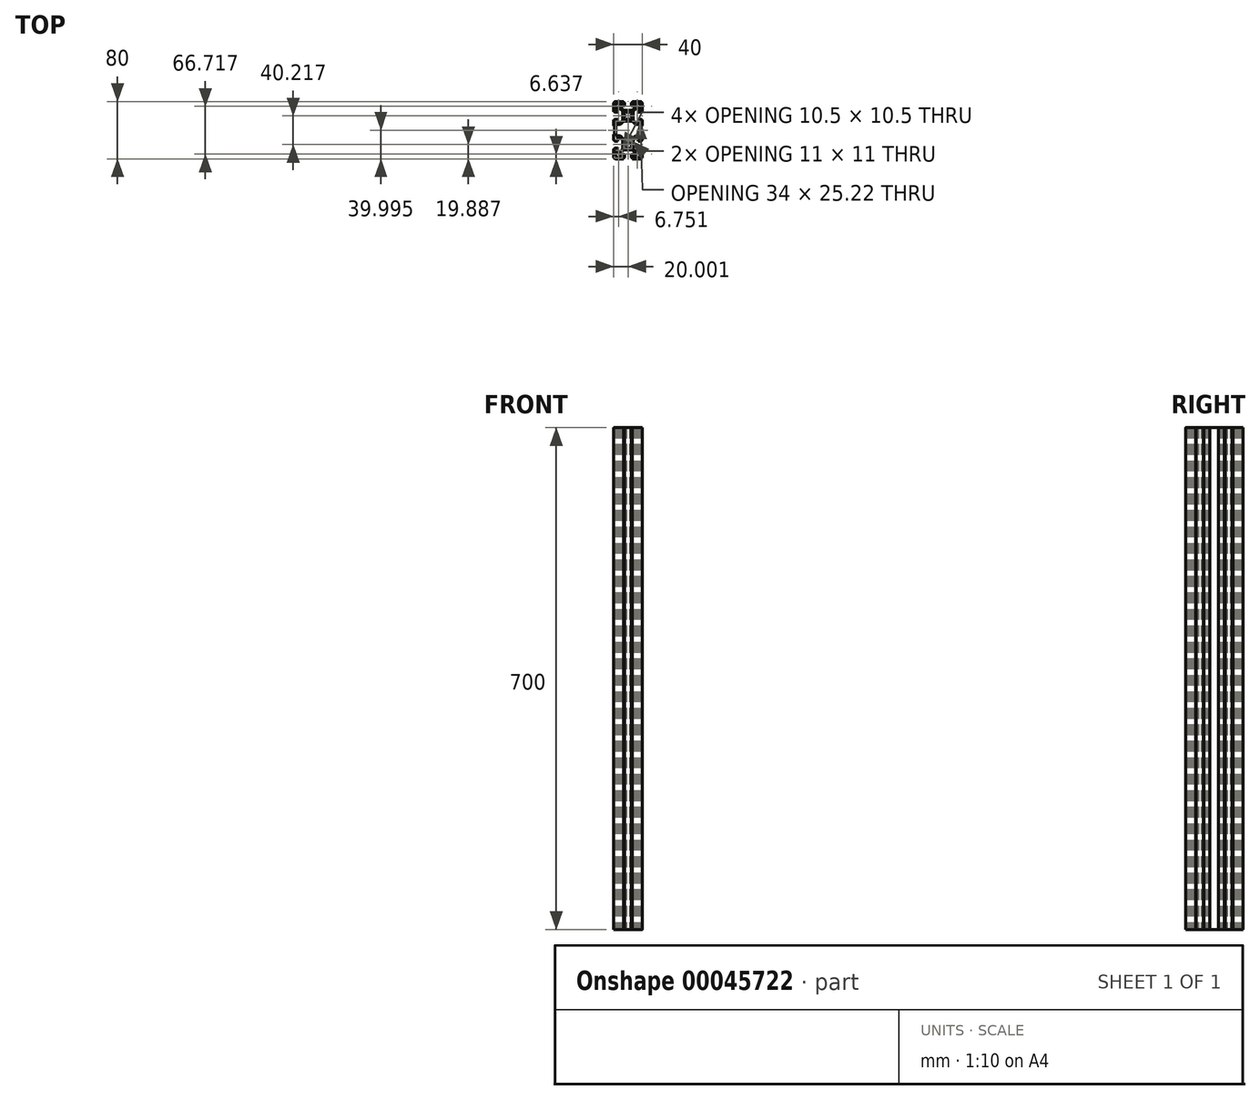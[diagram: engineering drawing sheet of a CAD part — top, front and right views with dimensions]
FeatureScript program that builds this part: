
annotation { "Feature Type Name" : "Feature", "Feature Type Description" : "" }
export const myFeature = defineFeature(function(context is Context, id is Id, definition is map)
    precondition{}
    {
        {
            var Q0;
            Q0=qCreatedBy(makeId("Top.planeOp"),FACE);
            var sketch = newSketch(context, id + "F0", { "sketchPlane" : qUnion([Q0])});
            skLineSegment(sketch, "E0", {"start": v(-19.67, 37.28) * mm, "end": v(-19.67, 26.18) * mm});
            skLineSegment(sketch, "E1", {"start": v(-19.67, 26.18) * mm, "end": v(-18.17, 26.18) * mm});
            skLineSegment(sketch, "E2", {"start": v(-18.17, 26.18) * mm, "end": v(-18.17, 25.38) * mm});
            skLineSegment(sketch, "E3", {"start": v(-18.17, 25.38) * mm, "end": v(-13.67, 25.38) * mm});
            skLineSegment(sketch, "E4", {"start": v(-13.67, 25.38) * mm, "end": v(-13.67, 30.43) * mm});
            skLineSegment(sketch, "E5", {"start": v(-13.67, 30.43) * mm, "end": v(-11.13, 30.43) * mm});
            skLineSegment(sketch, "E6", {"start": v(-11.13, 30.43) * mm, "end": v(-7.17, 26.47) * mm});
            skLineSegment(sketch, "E7", {"start": v(-7.17, 26.47) * mm, "end": v(-7.17, 14.3) * mm});
            skLineSegment(sketch, "E8", {"start": v(-7.17, 14.3) * mm, "end": v(-11.13, 10.33) * mm});
            skLineSegment(sketch, "E9", {"start": v(-11.13, 10.33) * mm, "end": v(-13.67, 10.33) * mm});
            skLineSegment(sketch, "E10", {"start": v(-13.67, 10.33) * mm, "end": v(-13.67, 15.38) * mm});
            skLineSegment(sketch, "E11", {"start": v(-13.67, 15.38) * mm, "end": v(-18.17, 15.38) * mm});
            skLineSegment(sketch, "E12", {"start": v(-18.17, 15.38) * mm, "end": v(-18.17, 14.58) * mm});
            skLineSegment(sketch, "E13", {"start": v(-18.17, 14.58) * mm, "end": v(-19.67, 14.58) * mm});
            skLineSegment(sketch, "E14", {"start": v(-19.67, 14.58) * mm, "end": v(-19.67, 6.38) * mm});
            skLineSegment(sketch, "E15", {"start": v(-19.67, 6.38) * mm, "end": v(-18.67, 6.38) * mm});
            skLineSegment(sketch, "E16", {"start": v(-18.67, 6.38) * mm, "end": v(-18.67, -5.83) * mm});
            skLineSegment(sketch, "E17", {"start": v(-18.67, -5.83) * mm, "end": v(-19.67, -5.83) * mm});
            skLineSegment(sketch, "E18", {"start": v(-19.67, -5.83) * mm, "end": v(-19.67, -14.03) * mm});
            skLineSegment(sketch, "E19", {"start": v(-19.67, -14.03) * mm, "end": v(-18.17, -14.03) * mm});
            skLineSegment(sketch, "E20", {"start": v(-18.17, -14.03) * mm, "end": v(-18.17, -14.83) * mm});
            skLineSegment(sketch, "E21", {"start": v(-18.17, -14.83) * mm, "end": v(-13.67, -14.83) * mm});
            skLineSegment(sketch, "E22", {"start": v(-13.67, -14.83) * mm, "end": v(-13.67, -9.78) * mm});
            skLineSegment(sketch, "E23", {"start": v(-13.67, -9.78) * mm, "end": v(-11.13, -9.78) * mm});
            skLineSegment(sketch, "E24", {"start": v(-11.13, -9.78) * mm, "end": v(-7.17, -13.75) * mm});
            skLineSegment(sketch, "E25", {"start": v(-7.17, -13.75) * mm, "end": v(-7.17, -25.92) * mm});
            skLineSegment(sketch, "E26", {"start": v(-7.17, -25.92) * mm, "end": v(-11.13, -29.88) * mm});
            skLineSegment(sketch, "E27", {"start": v(-11.13, -29.88) * mm, "end": v(-13.67, -29.88) * mm});
            skLineSegment(sketch, "E28", {"start": v(-13.67, -29.88) * mm, "end": v(-13.67, -24.83) * mm});
            skLineSegment(sketch, "E29", {"start": v(-13.67, -24.83) * mm, "end": v(-18.17, -24.83) * mm});
            skLineSegment(sketch, "E30", {"start": v(-18.17, -24.83) * mm, "end": v(-18.17, -25.63) * mm});
            skLineSegment(sketch, "E31", {"start": v(-18.17, -25.63) * mm, "end": v(-19.67, -25.63) * mm});
            skLineSegment(sketch, "E32", {"start": v(-19.67, -25.63) * mm, "end": v(-19.67, -36.72) * mm});
            skLineSegment(sketch, "E33", {"start": v(-16.67, -39.72) * mm, "end": v(-5.47, -39.72) * mm});
            skLineSegment(sketch, "E34", {"start": v(-5.47, -39.72) * mm, "end": v(-5.47, -38.22) * mm});
            skLineSegment(sketch, "E35", {"start": v(-5.47, -38.22) * mm, "end": v(-4.67, -38.22) * mm});
            skLineSegment(sketch, "E36", {"start": v(-4.67, -38.22) * mm, "end": v(-4.67, -33.72) * mm});
            skLineSegment(sketch, "E37", {"start": v(-4.67, -33.72) * mm, "end": v(-9.72, -33.72) * mm});
            skLineSegment(sketch, "E38", {"start": v(-9.72, -33.72) * mm, "end": v(-9.72, -31.19) * mm});
            skLineSegment(sketch, "E39", {"start": v(-9.72, -31.19) * mm, "end": v(-5.75, -27.22) * mm});
            skLineSegment(sketch, "E40", {"start": v(-5.75, -27.22) * mm, "end": v(6.42, -27.22) * mm});
            skLineSegment(sketch, "E41", {"start": v(6.42, -27.22) * mm, "end": v(10.38, -31.19) * mm});
            skLineSegment(sketch, "E42", {"start": v(10.38, -31.19) * mm, "end": v(10.38, -33.72) * mm});
            skLineSegment(sketch, "E43", {"start": v(10.38, -33.72) * mm, "end": v(5.33, -33.72) * mm});
            skLineSegment(sketch, "E44", {"start": v(5.33, -33.72) * mm, "end": v(5.33, -38.22) * mm});
            skLineSegment(sketch, "E45", {"start": v(5.33, -38.22) * mm, "end": v(6.13, -38.22) * mm});
            skLineSegment(sketch, "E46", {"start": v(6.13, -38.22) * mm, "end": v(6.13, -39.72) * mm});
            skLineSegment(sketch, "E47", {"start": v(6.13, -39.72) * mm, "end": v(17.33, -39.72) * mm});
            skLineSegment(sketch, "E48", {"start": v(20.33, -36.72) * mm, "end": v(20.33, -25.63) * mm});
            skLineSegment(sketch, "E49", {"start": v(20.33, -25.63) * mm, "end": v(18.83, -25.63) * mm});
            skLineSegment(sketch, "E50", {"start": v(18.83, -25.63) * mm, "end": v(18.83, -24.83) * mm});
            skLineSegment(sketch, "E51", {"start": v(18.83, -24.83) * mm, "end": v(14.33, -24.83) * mm});
            skLineSegment(sketch, "E52", {"start": v(14.33, -24.83) * mm, "end": v(14.33, -29.88) * mm});
            skLineSegment(sketch, "E53", {"start": v(14.33, -29.88) * mm, "end": v(11.8, -29.88) * mm});
            skLineSegment(sketch, "E54", {"start": v(11.8, -29.88) * mm, "end": v(7.83, -25.92) * mm});
            skLineSegment(sketch, "E55", {"start": v(7.83, -25.92) * mm, "end": v(7.83, -13.75) * mm});
            skLineSegment(sketch, "E56", {"start": v(7.83, -13.75) * mm, "end": v(11.8, -9.78) * mm});
            skLineSegment(sketch, "E57", {"start": v(11.8, -9.78) * mm, "end": v(14.33, -9.78) * mm});
            skLineSegment(sketch, "E58", {"start": v(14.33, -9.78) * mm, "end": v(14.33, -14.83) * mm});
            skLineSegment(sketch, "E59", {"start": v(14.33, -14.83) * mm, "end": v(18.83, -14.83) * mm});
            skLineSegment(sketch, "E60", {"start": v(18.83, -14.83) * mm, "end": v(18.83, -14.03) * mm});
            skLineSegment(sketch, "E61", {"start": v(18.83, -14.03) * mm, "end": v(20.33, -14.03) * mm});
            skLineSegment(sketch, "E62", {"start": v(20.33, -14.03) * mm, "end": v(20.33, -5.83) * mm});
            skLineSegment(sketch, "E63", {"start": v(20.33, -5.83) * mm, "end": v(19.33, -5.83) * mm});
            skLineSegment(sketch, "E64", {"start": v(19.33, -5.83) * mm, "end": v(19.33, 6.38) * mm});
            skLineSegment(sketch, "E65", {"start": v(19.33, 6.38) * mm, "end": v(20.33, 6.38) * mm});
            skLineSegment(sketch, "E66", {"start": v(20.33, 6.38) * mm, "end": v(20.33, 14.58) * mm});
            skLineSegment(sketch, "E67", {"start": v(20.33, 14.58) * mm, "end": v(18.83, 14.58) * mm});
            skLineSegment(sketch, "E68", {"start": v(18.83, 14.58) * mm, "end": v(18.83, 15.38) * mm});
            skLineSegment(sketch, "E69", {"start": v(18.83, 15.38) * mm, "end": v(14.33, 15.38) * mm});
            skLineSegment(sketch, "E70", {"start": v(14.33, 15.38) * mm, "end": v(14.33, 10.33) * mm});
            skLineSegment(sketch, "E71", {"start": v(14.33, 10.33) * mm, "end": v(11.8, 10.33) * mm});
            skLineSegment(sketch, "E72", {"start": v(11.8, 10.33) * mm, "end": v(7.83, 14.3) * mm});
            skLineSegment(sketch, "E73", {"start": v(7.83, 14.3) * mm, "end": v(7.83, 26.47) * mm});
            skLineSegment(sketch, "E74", {"start": v(7.83, 26.47) * mm, "end": v(11.8, 30.43) * mm});
            skLineSegment(sketch, "E75", {"start": v(11.8, 30.43) * mm, "end": v(14.33, 30.43) * mm});
            skLineSegment(sketch, "E76", {"start": v(14.33, 30.43) * mm, "end": v(14.33, 25.38) * mm});
            skLineSegment(sketch, "E77", {"start": v(14.33, 25.38) * mm, "end": v(18.83, 25.38) * mm});
            skLineSegment(sketch, "E78", {"start": v(18.83, 25.38) * mm, "end": v(18.83, 26.18) * mm});
            skLineSegment(sketch, "E79", {"start": v(18.83, 26.18) * mm, "end": v(20.33, 26.18) * mm});
            skLineSegment(sketch, "E80", {"start": v(20.33, 26.18) * mm, "end": v(20.33, 37.28) * mm});
            skLineSegment(sketch, "E81", {"start": v(17.33, 40.28) * mm, "end": v(6.13, 40.28) * mm});
            skLineSegment(sketch, "E82", {"start": v(6.13, 40.28) * mm, "end": v(6.13, 38.78) * mm});
            skLineSegment(sketch, "E83", {"start": v(6.13, 38.78) * mm, "end": v(5.33, 38.78) * mm});
            skLineSegment(sketch, "E84", {"start": v(5.33, 38.78) * mm, "end": v(5.33, 34.28) * mm});
            skLineSegment(sketch, "E85", {"start": v(5.33, 34.28) * mm, "end": v(10.38, 34.28) * mm});
            skLineSegment(sketch, "E86", {"start": v(10.38, 34.28) * mm, "end": v(10.38, 31.74) * mm});
            skLineSegment(sketch, "E87", {"start": v(10.38, 31.74) * mm, "end": v(6.42, 27.78) * mm});
            skLineSegment(sketch, "E88", {"start": v(6.42, 27.78) * mm, "end": v(-5.75, 27.78) * mm});
            skLineSegment(sketch, "E89", {"start": v(-5.75, 27.78) * mm, "end": v(-9.72, 31.74) * mm});
            skLineSegment(sketch, "E90", {"start": v(-9.72, 31.74) * mm, "end": v(-9.72, 34.28) * mm});
            skLineSegment(sketch, "E91", {"start": v(-9.72, 34.28) * mm, "end": v(-4.67, 34.28) * mm});
            skLineSegment(sketch, "E92", {"start": v(-4.67, 34.28) * mm, "end": v(-4.67, 38.78) * mm});
            skLineSegment(sketch, "E93", {"start": v(-4.67, 38.78) * mm, "end": v(-5.47, 38.78) * mm});
            skLineSegment(sketch, "E94", {"start": v(-5.47, 38.78) * mm, "end": v(-5.47, 40.28) * mm});
            skLineSegment(sketch, "E95", {"start": v(-5.47, 40.28) * mm, "end": v(-16.67, 40.28) * mm});
            skLineSegment(sketch, "E96", {"start": v(-14.17, 37.63) * mm, "end": v(-14.17, 38.88) * mm});
            skLineSegment(sketch, "E97", {"start": v(-14.17, 38.88) * mm, "end": v(-9.17, 38.88) * mm});
            skLineSegment(sketch, "E98", {"start": v(-9.17, 35.88) * mm, "end": v(-11.42, 35.88) * mm});
            skLineSegment(sketch, "E99", {"start": v(-15.17, 32.13) * mm, "end": v(-15.17, 29.88) * mm});
            skLineSegment(sketch, "E100", {"start": v(-16.92, 34.88) * mm, "end": v(-18.17, 34.88) * mm});
            skLineSegment(sketch, "E101", {"start": v(-18.17, 34.88) * mm, "end": v(-18.17, 29.88) * mm});
            skArc(sketch, "E102", {"start": v(-9.17, 35.88) * mm, "mid": v(-7.67, 37.38) * mm, "end": v(-9.17, 38.88) * mm});
            skArc(sketch, "E103", {"start": v(-18.17, 29.88) * mm, "mid": v(-16.67, 28.38) * mm, "end": v(-15.17, 29.88) * mm});
            skArc(sketch, "E104", {"start": v(-14.17, 37.63) * mm, "mid": v(-16.11, 36.83) * mm, "end": v(-16.92, 34.88) * mm});
            skArc(sketch, "E105", {"start": v(9.83, 38.88) * mm, "mid": v(8.33, 37.38) * mm, "end": v(9.83, 35.88) * mm});
            skArc(sketch, "E106", {"start": v(15.83, 29.88) * mm, "mid": v(17.33, 28.38) * mm, "end": v(18.83, 29.88) * mm});
            skArc(sketch, "E107", {"start": v(-4.25, 22.38) * mm, "mid": v(-4.67, 20.38) * mm, "end": v(-4.25, 18.39) * mm});
            skArc(sketch, "E108", {"start": v(-11.6, -35.33) * mm, "mid": v(-12.22, -32.39) * mm, "end": v(-15.17, -31.77) * mm});
            skArc(sketch, "E109", {"start": v(14.83, -37.08) * mm, "mid": v(16.78, -36.28) * mm, "end": v(17.58, -34.33) * mm});
            skArc(sketch, "E110", {"start": v(9.83, -35.33) * mm, "mid": v(8.33, -36.83) * mm, "end": v(9.83, -38.33) * mm});
            skArc(sketch, "E111", {"start": v(18.83, -29.33) * mm, "mid": v(17.33, -27.83) * mm, "end": v(15.83, -29.33) * mm});
            skArc(sketch, "E112", {"start": v(12.27, 35.88) * mm, "mid": v(12.89, 32.94) * mm, "end": v(15.83, 32.32) * mm});
            skLineSegment(sketch, "E113", {"start": v(-15.17, 32.13) * mm, "end": v(-15.17, 32.32) * mm});
            skLineSegment(sketch, "E114", {"start": v(-11.42, 35.88) * mm, "end": v(-11.6, 35.88) * mm});
            skLineSegment(sketch, "E115", {"start": v(9.83, 38.88) * mm, "end": v(14.83, 38.88) * mm});
            skLineSegment(sketch, "E116", {"start": v(14.83, 38.88) * mm, "end": v(14.83, 37.63) * mm});
            skLineSegment(sketch, "E117", {"start": v(9.83, 35.88) * mm, "end": v(12.27, 35.88) * mm});
            skLineSegment(sketch, "E118", {"start": v(17.58, 34.88) * mm, "end": v(18.83, 34.88) * mm});
            skLineSegment(sketch, "E119", {"start": v(18.83, 34.88) * mm, "end": v(18.83, 29.88) * mm});
            skLineSegment(sketch, "E120", {"start": v(15.83, 29.88) * mm, "end": v(15.83, 32.32) * mm});
            skArc(sketch, "E121.trimOffspring", {"start": v(17.58, 34.88) * mm, "mid": v(16.78, 36.83) * mm, "end": v(14.83, 37.63) * mm});
            skArc(sketch, "E122.trimOffspring", {"start": v(-15.17, 32.32) * mm, "mid": v(-12.22, 32.94) * mm, "end": v(-11.6, 35.88) * mm});
            skLineSegment(sketch, "E123", {"start": v(-4.25, 22.38) * mm, "end": v(-5.17, 22.78) * mm});
            skLineSegment(sketch, "E124", {"start": v(-5.17, 22.78) * mm, "end": v(-5.17, 25.88) * mm});
            skLineSegment(sketch, "E125", {"start": v(-5.17, 25.88) * mm, "end": v(-2.07, 25.88) * mm});
            skLineSegment(sketch, "E126", {"start": v(-2.07, 25.88) * mm, "end": v(-1.67, 24.97) * mm});
            skLineSegment(sketch, "E127", {"start": v(2.33, 24.97) * mm, "end": v(2.73, 25.88) * mm});
            skLineSegment(sketch, "E128", {"start": v(2.73, 25.88) * mm, "end": v(5.83, 25.88) * mm});
            skLineSegment(sketch, "E129", {"start": v(5.83, 25.88) * mm, "end": v(5.83, 22.78) * mm});
            skLineSegment(sketch, "E130", {"start": v(-4.25, 18.39) * mm, "end": v(-5.17, 17.99) * mm});
            skLineSegment(sketch, "E131", {"start": v(-5.17, 17.99) * mm, "end": v(-5.17, 14.88) * mm});
            skLineSegment(sketch, "E132", {"start": v(-5.17, 14.88) * mm, "end": v(-2.07, 14.88) * mm});
            skLineSegment(sketch, "E133", {"start": v(-2.07, 14.88) * mm, "end": v(-1.67, 15.8) * mm});
            skLineSegment(sketch, "E134", {"start": v(2.33, 15.8) * mm, "end": v(2.73, 14.88) * mm});
            skLineSegment(sketch, "E135", {"start": v(2.73, 14.88) * mm, "end": v(5.83, 14.88) * mm});
            skLineSegment(sketch, "E136", {"start": v(5.83, 14.88) * mm, "end": v(5.83, 17.99) * mm});
            skArc(sketch, "E137.trimOffspring", {"start": v(2.33, 24.97) * mm, "mid": v(0.33, 25.38) * mm, "end": v(-1.67, 24.97) * mm});
            skArc(sketch, "E138.trimOffspring", {"start": v(4.91, 18.39) * mm, "mid": v(5.33, 20.38) * mm, "end": v(4.91, 22.38) * mm});
            skLineSegment(sketch, "E139", {"start": v(-16.67, 8.33) * mm, "end": v(-16.67, -7.78) * mm});
            skLineSegment(sketch, "E140", {"start": v(-16.67, -7.78) * mm, "end": v(-10.3, -7.78) * mm});
            skLineSegment(sketch, "E141", {"start": v(-10.3, -7.78) * mm, "end": v(-5.75, -12.33) * mm});
            skLineSegment(sketch, "E142", {"start": v(-5.75, -12.33) * mm, "end": v(6.42, -12.33) * mm});
            skLineSegment(sketch, "E143", {"start": v(6.42, -12.33) * mm, "end": v(10.97, -7.78) * mm});
            skLineSegment(sketch, "E144", {"start": v(10.97, -7.78) * mm, "end": v(17.33, -7.78) * mm});
            skLineSegment(sketch, "E145", {"start": v(17.33, -7.78) * mm, "end": v(17.33, 8.33) * mm});
            skLineSegment(sketch, "E146", {"start": v(17.33, 8.33) * mm, "end": v(10.97, 8.33) * mm});
            skLineSegment(sketch, "E147", {"start": v(10.97, 8.33) * mm, "end": v(6.42, 12.88) * mm});
            skLineSegment(sketch, "E148", {"start": v(6.42, 12.88) * mm, "end": v(-5.75, 12.88) * mm});
            skLineSegment(sketch, "E149", {"start": v(-5.75, 12.88) * mm, "end": v(-10.3, 8.33) * mm});
            skLineSegment(sketch, "E150", {"start": v(-10.3, 8.33) * mm, "end": v(-16.67, 8.33) * mm});
            skLineSegment(sketch, "E151", {"start": v(-1.67, -15.25) * mm, "end": v(-2.07, -14.33) * mm});
            skLineSegment(sketch, "E152", {"start": v(-2.07, -14.33) * mm, "end": v(-5.17, -14.33) * mm});
            skLineSegment(sketch, "E153", {"start": v(-5.17, -14.33) * mm, "end": v(-5.17, -17.44) * mm});
            skLineSegment(sketch, "E154", {"start": v(-5.17, -17.44) * mm, "end": v(-4.25, -17.84) * mm});
            skLineSegment(sketch, "E155", {"start": v(2.33, -15.25) * mm, "end": v(2.73, -14.33) * mm});
            skLineSegment(sketch, "E156", {"start": v(2.73, -14.33) * mm, "end": v(5.83, -14.33) * mm});
            skLineSegment(sketch, "E157", {"start": v(5.83, -14.33) * mm, "end": v(5.83, -17.44) * mm});
            skLineSegment(sketch, "E158", {"start": v(5.83, -17.44) * mm, "end": v(4.91, -17.84) * mm});
            skLineSegment(sketch, "E159", {"start": v(-4.25, -21.83) * mm, "end": v(-5.17, -22.23) * mm});
            skLineSegment(sketch, "E160", {"start": v(-5.17, -22.23) * mm, "end": v(-5.17, -25.33) * mm});
            skLineSegment(sketch, "E161", {"start": v(-5.17, -25.33) * mm, "end": v(-2.07, -25.33) * mm});
            skLineSegment(sketch, "E162", {"start": v(-2.07, -25.33) * mm, "end": v(-1.67, -24.42) * mm});
            skLineSegment(sketch, "E163", {"start": v(2.33, -24.42) * mm, "end": v(2.73, -25.33) * mm});
            skLineSegment(sketch, "E164", {"start": v(2.73, -25.33) * mm, "end": v(5.83, -25.33) * mm});
            skLineSegment(sketch, "E165", {"start": v(5.83, -25.33) * mm, "end": v(5.83, -22.23) * mm});
            skLineSegment(sketch, "E166", {"start": v(5.83, -22.23) * mm, "end": v(4.91, -21.83) * mm});
            skLineSegment(sketch, "E167", {"start": v(-18.17, -29.33) * mm, "end": v(-18.17, -34.33) * mm});
            skLineSegment(sketch, "E168", {"start": v(-18.17, -34.33) * mm, "end": v(-16.92, -34.33) * mm});
            skLineSegment(sketch, "E169", {"start": v(-15.17, -29.33) * mm, "end": v(-15.17, -31.77) * mm});
            skLineSegment(sketch, "E170", {"start": v(-11.42, -34.33) * mm, "end": v(-11.42, -35.33) * mm});
            skLineSegment(sketch, "E171", {"start": v(-9.17, -35.33) * mm, "end": v(-11.6, -35.33) * mm});
            skLineSegment(sketch, "E172", {"start": v(-14.17, -37.08) * mm, "end": v(-14.17, -38.33) * mm});
            skLineSegment(sketch, "E173", {"start": v(-14.17, -38.33) * mm, "end": v(-9.17, -38.33) * mm});
            skLineSegment(sketch, "E174", {"start": v(9.83, -35.33) * mm, "end": v(12.27, -35.33) * mm});
            skLineSegment(sketch, "E175", {"start": v(9.83, -38.33) * mm, "end": v(14.83, -38.33) * mm});
            skLineSegment(sketch, "E176", {"start": v(14.83, -38.33) * mm, "end": v(14.83, -37.08) * mm});
            skLineSegment(sketch, "E177", {"start": v(17.58, -34.33) * mm, "end": v(18.83, -34.33) * mm});
            skLineSegment(sketch, "E178", {"start": v(18.83, -34.33) * mm, "end": v(18.83, -29.33) * mm});
            skLineSegment(sketch, "E179", {"start": v(15.83, -29.33) * mm, "end": v(15.83, -31.77) * mm});
            skArc(sketch, "E180.trimOffspring", {"start": v(15.83, -31.77) * mm, "mid": v(12.89, -32.39) * mm, "end": v(12.27, -35.33) * mm});
            skLineSegment(sketch, "E181", {"start": v(4.91, 18.39) * mm, "end": v(5.83, 17.99) * mm});
            skLineSegment(sketch, "E182", {"start": v(4.91, 22.38) * mm, "end": v(5.83, 22.78) * mm});
            skPoint(sketch, "E183.center.orphan", {"position": v(0.33, -19.83) * mm});
            skPoint(sketch, "E184.center.orphan", {"position": v(-16.67, -29.33) * mm});
            skPoint(sketch, "E185.center.orphan", {"position": v(-9.17, -36.83) * mm});
            skArc(sketch, "E186", {"start": v(-19.67, -36.72) * mm, "mid": v(-18.8, -38.85) * mm, "end": v(-16.67, -39.72) * mm});
            skArc(sketch, "E187", {"start": v(17.33, -39.72) * mm, "mid": v(19.45, -38.85) * mm, "end": v(20.33, -36.72) * mm});
            skArc(sketch, "E188", {"start": v(20.33, 37.28) * mm, "mid": v(19.45, 39.4) * mm, "end": v(17.33, 40.28) * mm});
            skArc(sketch, "E189", {"start": v(-19.67, 37.28) * mm, "mid": v(-18.8, 39.4) * mm, "end": v(-16.67, 40.28) * mm});
            skArc(sketch, "E190", {"start": v(-1.67, 15.8) * mm, "mid": v(0.33, 15.38) * mm, "end": v(2.33, 15.8) * mm});
            skArc(sketch, "E191", {"start": v(-4.25, -17.84) * mm, "mid": v(-4.67, -19.83) * mm, "end": v(-4.25, -21.83) * mm});
            skArc(sketch, "E192", {"start": v(-1.67, -15.25) * mm, "mid": v(0.33, -14.83) * mm, "end": v(2.33, -15.25) * mm});
            skArc(sketch, "E193", {"start": v(4.91, -17.84) * mm, "mid": v(5.33, -19.83) * mm, "end": v(4.91, -21.83) * mm});
            skArc(sketch, "E194", {"start": v(2.33, -24.42) * mm, "mid": v(0.33, -24.83) * mm, "end": v(-1.67, -24.42) * mm});
            skArc(sketch, "E195", {"start": v(-18.17, -29.33) * mm, "mid": v(-16.67, -27.83) * mm, "end": v(-15.17, -29.33) * mm});
            skArc(sketch, "E196", {"start": v(-9.17, -35.33) * mm, "mid": v(-7.67, -36.83) * mm, "end": v(-9.17, -38.33) * mm});
            skArc(sketch, "E197", {"start": v(-16.92, -34.33) * mm, "mid": v(-16.11, -36.28) * mm, "end": v(-14.17, -37.08) * mm});
            skSolve(sketch);
        }
        {
            var Q0;
            Q0 = qSketchRegion(id + "F0", true);
            extrude(context, id + "F1", {"entities" : qUnion([Q0]), "depth" : 700 * mm});
        }
    });
